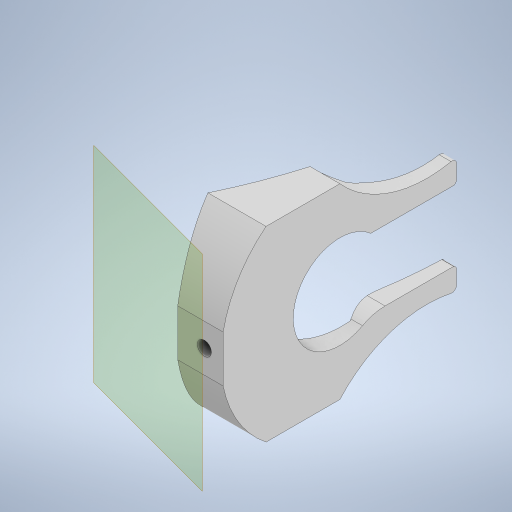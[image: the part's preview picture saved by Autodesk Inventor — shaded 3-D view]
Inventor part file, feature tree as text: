
AUTODESK INVENTOR PART (.ipt)
format: ipt  version: 2024.2 (Build 282272000, 272)  size: 395,264 bytes
history: native  units: mm
features: extrude x5, sketch x5, fillet x2, plane x1
ambient origin geometry x8: Origin, YZ Plane, XZ Plane, XY Plane, X Axis, Y Axis, Z Axis, Center Point
bodies: Solid1 (feature_tree)
feature tree (13):
  extrude  "Extrusion1"  Depth=80.0mm TaperAngle=0.0deg
  extrude  "Extrusion2"  Depth=5.0mm
  extrude  "Extrusion3"  Depth=20.0mm
  plane  "Work Plane2"
  extrude  "Extrusion4"  Depth=50.0mm
  fillet  "Fillet1"  Radius=10.0mm
  extrude  "Extrusion5"  Depth=10.0mm
  fillet  "Fillet2"  Radius=80.0mm
  sketch  "Sketch1"  dims[d0=35.0mm d1=100.0mm d3=80.0mm d4=0.0mm]
  sketch  "Sketch2"  dims[d5=200.0mm d6=5.0mm]
  sketch  "Sketch3"  dims[d7=40.0mm d8=20.0mm]
  sketch  "Sketch5"  dims[d9=30.0mm d13=50.0mm d14=10.0mm]
  sketch  "Sketch6"  dims[d15=50.0mm d16=10.0mm d17=80.0mm d18=0.0mm d19=6.0mm d20=8.0mm d21=0.0mm d22=0.0mm d29=165.0deg d30=10.0mm d31=80.0mm d32=65.0mm d33=65.0mm d34=10.0mm d35=65.0mm d36=0.0mm d37=20.0mm d38=65.0mm d39=0.0mm d40=2.0mm]
